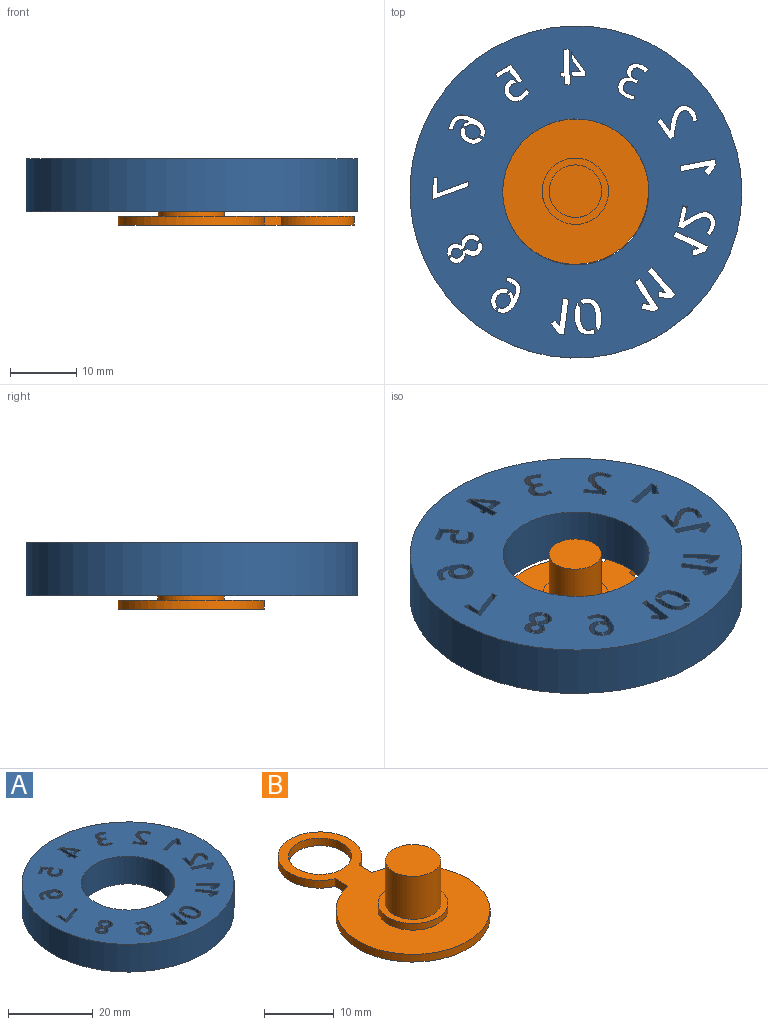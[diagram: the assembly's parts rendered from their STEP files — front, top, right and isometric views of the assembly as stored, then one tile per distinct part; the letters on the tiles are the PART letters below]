
ASSEMBLY  parts=2 mates=1
PART A: 389 faces, bbox 50x50x8 mm
  f0: plane 50x50mm, normal (0,0,1), area 1468.7mm2, adj f2,f3,f4,f5,f6,f7,f8,f9
  f1: plane 50x50mm, normal (0,0,-1), area 1468.7mm2, adj f2,f3,f4,f5,f6,f7,f8,f9
  f2: cylinder r=11mm len=22mm, axis (0,0,-1), area 552.9mm2, adj f0,f1
  f3: cylinder r=25mm len=50mm, axis (0,0,-1), area 1256.6mm2, adj f0,f1
  f4: plane 8x1.59mm, normal (-0.83,0.56,0), area 15.4mm2, adj f0,f1,f5,f10
  f5: plane 8x0.73mm, normal (0.56,0.83,0), area 7.1mm2, adj f0,f1,f4,f6
  f6: plane 8x0.86mm, normal (0.83,-0.56,0), area 8.3mm2, adj f0,f1,f5,f7
  f7: plane 8x4.05mm, normal (-0.19,0.98,0), area 33mm2, adj f0,f1,f6,f8
  f8: plane 8x0.88mm, normal (0.98,0.19,0), area 7.1mm2, adj f0,f1,f7,f9
  f9: plane 8x5.28mm, normal (0.19,-0.98,0), area 43mm2, adj f0,f1,f8,f10
  f10: plane 8x0.88mm, normal (-0.98,-0.19,0), area 7.1mm2, adj f0,f1,f4,f9
  f11: plane 8x1.81mm, normal (-0.34,0.94,0), area 15.4mm2, adj f0,f1,f12,f17
  f12: plane 8x0.83mm, normal (0.94,0.34,0), area 7.1mm2, adj f0,f1,f11,f13
  f13: plane 8x0.98mm, normal (0.34,-0.94,0), area 8.3mm2, adj f0,f1,f12,f14
  f14: plane 8x3.74mm, normal (0.42,0.91,0), area 33mm2, adj f0,f1,f13,f15
  f15: plane 8x0.81mm, normal (0.91,-0.42,0), area 7.1mm2, adj f0,f1,f14,f16
  f16: plane 8x4.87mm, normal (-0.42,-0.91,0), area 43mm2, adj f0,f1,f15,f17
  f17: plane 8x0.81mm, normal (-0.91,0.42,0), area 7.1mm2, adj f0,f1,f11,f16
  f18: plane 8x0.47mm, normal (0.63,0.78,0), area 4.8mm2, adj f0,f1,f28,f29
  f19: plane 8x0.79mm, normal (0.23,0.97,0), area 6.5mm2, adj f0,f1,f20,f42
  f20: plane 8x3.25mm, normal (0.97,-0.23,0), area 26.7mm2, adj f0,f1,f19,f21
  f21: plane 8x0.69mm, normal (-0.23,-0.97,0), area 5.7mm2, adj f0,f1,f20,f22
  f22: plane 8x2.22mm, normal (-0.97,0.23,0), area 18.3mm2, adj f0,f1,f21,f43
  f23: extruded ~8x0.63mm, area 5.5mm2, adj f0,f1,f24,f50
  f24: extruded ~8x0.83mm, area 6.7mm2, adj f0,f1,f23,f25
  f25: extruded ~8x0.36mm, area 3mm2, adj f0,f1,f24,f26
  f26: extruded ~8x0.38mm, area 3.4mm2, adj f0,f1,f25,f27
  f27: extruded ~8x0.36mm, area 3.4mm2, adj f0,f1,f26,f28
  f28: extruded ~8x0.28mm, area 3.1mm2, adj f0,f1,f18,f27
  f29: extruded ~8x0.2mm, area 2.1mm2, adj f0,f1,f18,f30
  f30: extruded ~8x0.22mm, area 2.1mm2, adj f0,f1,f29,f31
  f31: extruded ~8x0.3mm, area 2.6mm2, adj f0,f1,f30,f32
  f32: extruded ~8x0.45mm, area 3.8mm2, adj f0,f1,f31,f33
  f33: extruded ~8x0.31mm, area 2.5mm2, adj f0,f1,f32,f34
  f34: extruded ~8x0.33mm, area 2.7mm2, adj f0,f1,f33,f35
  f35: extruded ~8x0.29mm, area 2.9mm2, adj f0,f1,f34,f36
  f36: extruded ~8x0.39mm, area 3.5mm2, adj f0,f1,f35,f37
  f37: extruded ~8x0.54mm, area 4.4mm2, adj f0,f1,f36,f38
  f38: extruded ~8x0.63mm, area 5.4mm2, adj f0,f1,f37,f39
  f39: extruded ~8x0.67mm, area 6mm2, adj f0,f1,f38,f40
  f40: extruded ~8x0.64mm, area 6mm2, adj f0,f1,f39,f41
  f41: extruded ~8x0.55mm, area 5.4mm2, adj f0,f1,f40,f42
  f42: extruded ~8x0.39mm, area 3.9mm2, adj f0,f1,f19,f41
  f43: extruded ~8x0.41mm, area 3.9mm2, adj f0,f1,f22,f44
  f44: extruded ~8x0.54mm, area 5.1mm2, adj f0,f1,f43,f45
  f45: extruded ~8x0.62mm, area 5.7mm2, adj f0,f1,f44,f46
  f46: extruded ~8x0.66mm, area 5.8mm2, adj f0,f1,f45,f47
  f47: extruded ~8x0.66mm, area 5.5mm2, adj f0,f1,f46,f48
  f48: extruded ~8x0.6mm, area 4.8mm2, adj f0,f1,f47,f49
  f49: extruded ~8x0.52mm, area 4.6mm2, adj f0,f1,f48,f50
  f50: extruded ~8x0.44mm, area 5mm2, adj f0,f1,f23,f49
  f51: plane 8x1.89mm, normal (0.21,0.98,0), area 15.4mm2, adj f0,f1,f52,f57
  f52: plane 8x0.87mm, normal (0.98,-0.21,0), area 7.1mm2, adj f0,f1,f51,f53
  f53: plane 8x1.02mm, normal (-0.21,-0.98,0), area 8.3mm2, adj f0,f1,f52,f54
  f54: plane 8x3.46mm, normal (0.84,0.54,0), area 33mm2, adj f0,f1,f53,f55
  f55: plane 8x0.75mm, normal (0.54,-0.84,0), area 7.1mm2, adj f0,f1,f54,f56
  f56: plane 8x4.52mm, normal (-0.84,-0.54,0), area 43mm2, adj f0,f1,f55,f57
  f57: plane 8x0.75mm, normal (-0.54,0.84,0), area 7.1mm2, adj f0,f1,f51,f56
  f58: plane 8x1.93mm, normal (0.06,1,0), area 15.4mm2, adj f0,f1,f59,f64
  f59: plane 8x0.89mm, normal (1,-0.06,0), area 7.1mm2, adj f0,f1,f58,f60
  f60: plane 8x1.04mm, normal (-0.06,-1,0), area 8.3mm2, adj f0,f1,f59,f61
  f61: plane 8x3.08mm, normal (0.75,0.66,0), area 33mm2, adj f0,f1,f60,f62
  f62: plane 8x0.67mm, normal (0.66,-0.75,0), area 7.1mm2, adj f0,f1,f61,f63
  f63: plane 8x4.02mm, normal (-0.75,-0.66,0), area 43mm2, adj f0,f1,f62,f64
  f64: plane 8x0.67mm, normal (-0.66,0.75,0), area 7.1mm2, adj f0,f1,f58,f63
  f65: plane 8x0.59mm, normal (-0.83,0.56,0), area 5.7mm2, adj f0,f1,f69,f70
  f66: plane 8x0.55mm, normal (-0.83,0.56,0), area 5.3mm2, adj f0,f1,f77,f78
  f67: extruded ~8x0.62mm, area 6.5mm2, adj f0,f1,f68,f78
  f68: extruded ~8x0.78mm, area 6.6mm2, adj f0,f1,f67,f69
  f69: extruded ~8x0.66mm, area 5.9mm2, adj f0,f1,f65,f68
  f70: extruded ~8x0.42mm, area 4.5mm2, adj f0,f1,f65,f71
  f71: extruded ~8x0.57mm, area 5mm2, adj f0,f1,f70,f72
  f72: extruded ~8x0.71mm, area 5.7mm2, adj f0,f1,f71,f73
  f73: extruded ~8x0.82mm, area 7.2mm2, adj f0,f1,f72,f74
  f74: extruded ~8x0.44mm, area 4.9mm2, adj f0,f1,f73,f75
  f75: extruded ~8x0.57mm, area 5.1mm2, adj f0,f1,f74,f76
  f76: extruded ~8x0.65mm, area 5.2mm2, adj f0,f1,f75,f77
  f77: extruded ~8x0.65mm, area 5.6mm2, adj f0,f1,f66,f76
  f78: extruded ~8x0.71mm, area 5.8mm2, adj f0,f1,f66,f67
  f79: plane 8x0.63mm, normal (0.46,-0.89,0), area 5.7mm2, adj f0,f1,f87,f88
  f80: plane 8x0.81mm, normal (0.46,-0.89,0), area 7.2mm2, adj f0,f1,f92,f93
  f81: plane 8x0.62mm, normal (0.46,-0.89,0), area 5.5mm2, adj f0,f1,f98,f99
  f82: extruded ~8x0.3mm, area 2.9mm2, adj f0,f1,f83,f108
  f83: extruded ~8x0.27mm, area 2.8mm2, adj f0,f1,f82,f84
  f84: extruded ~8x0.48mm, area 4.1mm2, adj f0,f1,f83,f85
  f85: extruded ~8x0.49mm, area 4mm2, adj f0,f1,f84,f86
  f86: extruded ~8x0.47mm, area 4.2mm2, adj f0,f1,f85,f87
  f87: extruded ~8x0.49mm, area 5.1mm2, adj f0,f1,f79,f86
  f88: extruded ~8x0.34mm, area 3.7mm2, adj f0,f1,f79,f89
  f89: extruded ~8x0.55mm, area 4.6mm2, adj f0,f1,f88,f90
  f90: extruded ~8x0.39mm, area 4.5mm2, adj f0,f1,f89,f91
  f91: extruded ~8x0.49mm, area 4.1mm2, adj f0,f1,f90,f92
  f92: extruded ~8x0.09mm, area 0.8mm2, adj f0,f1,f80,f91
  f93: extruded ~8x0.62mm, area 5.5mm2, adj f0,f1,f80,f94
  f94: extruded ~8x0.56mm, area 4.6mm2, adj f0,f1,f93,f95
  f95: extruded ~8x0.19mm, area 2mm2, adj f0,f1,f94,f96
  f96: extruded ~8x0.24mm, area 2.2mm2, adj f0,f1,f95,f97
  f97: extruded ~8x0.29mm, area 2.3mm2, adj f0,f1,f96,f98
  f98: extruded ~8x0.31mm, area 2.5mm2, adj f0,f1,f81,f97
  f99: extruded ~8x0.59mm, area 4.9mm2, adj f0,f1,f81,f100
  f100: extruded ~8x0.58mm, area 4.6mm2, adj f0,f1,f99,f101
  f101: extruded ~8x0.51mm, area 4.6mm2, adj f0,f1,f100,f102
  f102: extruded ~8x0.48mm, area 5mm2, adj f0,f1,f101,f103
  f103: extruded ~8x0.43mm, area 3.6mm2, adj f0,f1,f102,f104
  f104: extruded ~8x0.43mm, area 3.5mm2, adj f0,f1,f103,f105
  f105: extruded ~8x0.42mm, area 3.6mm2, adj f0,f1,f104,f106
  f106: extruded ~8x0.41mm, area 3.7mm2, adj f0,f1,f105,f107
  f107: extruded ~8x0.37mm, area 3mm2, adj f0,f1,f106,f108
  f108: extruded ~8x0.36mm, area 3.1mm2, adj f0,f1,f82,f107
  f109: plane 8x0.62mm, normal (-0.46,0.89,0), area 5.5mm2, adj f0,f1,f116,f117
  f110: plane 8x0.11mm, normal (-0.55,-0.83,0), area 1.1mm2, adj f0,f1,f111,f122
  f111: plane 8x0.79mm, normal (-0.46,0.89,0), area 7.1mm2, adj f0,f1,f110,f123
  f112: plane 8x0.63mm, normal (-0.46,0.89,0), area 5.7mm2, adj f0,f1,f126,f127
  f113: extruded ~8x0.84mm, area 7mm2, adj f0,f1,f114,f132
  f114: extruded ~8x0.69mm, area 7.7mm2, adj f0,f1,f113,f115
  f115: extruded ~8x1.1mm, area 9.1mm2, adj f0,f1,f114,f116
  f116: extruded ~8x0.9mm, area 10mm2, adj f0,f1,f109,f115
  f117: extruded ~8x0.5mm, area 5mm2, adj f0,f1,f109,f118
  f118: extruded ~8x0.57mm, area 4.7mm2, adj f0,f1,f117,f119
  f119: extruded ~8x0.29mm, area 3mm2, adj f0,f1,f118,f120
  f120: extruded ~8x0.28mm, area 2.7mm2, adj f0,f1,f119,f121
  f121: extruded ~8x0.29mm, area 2.5mm2, adj f0,f1,f120,f122
  f122: extruded ~8x0.27mm, area 2.2mm2, adj f0,f1,f110,f121
  f123: extruded ~8x0.48mm, area 4.4mm2, adj f0,f1,f111,f124
  f124: extruded ~8x0.4mm, area 3.3mm2, adj f0,f1,f123,f125
  f125: extruded ~8x0.37mm, area 4.2mm2, adj f0,f1,f124,f126
  f126: extruded ~8x0.5mm, area 4.1mm2, adj f0,f1,f112,f125
  f127: extruded ~8x0.54mm, area 4.5mm2, adj f0,f1,f112,f128
  f128: extruded ~8x0.51mm, area 4.1mm2, adj f0,f1,f127,f129
  f129: extruded ~8x0.45mm, area 4.1mm2, adj f0,f1,f128,f130
  f130: extruded ~8x0.45mm, area 4.6mm2, adj f0,f1,f129,f131
  f131: extruded ~8x0.69mm, area 5.7mm2, adj f0,f1,f130,f132
  f132: extruded ~8x0.69mm, area 5.9mm2, adj f0,f1,f113,f131
  f133: plane 8x3.38mm, normal (1,-0.02,0), area 27mm2, adj f0,f1,f134,f138
  f134: plane 8x0.71mm, normal (-0.02,-1,0), area 5.7mm2, adj f0,f1,f133,f135
  f135: plane 8x2.34mm, normal (-1,0.02,0), area 18.7mm2, adj f0,f1,f134,f136
  f136: plane 8x4.71mm, normal (0.35,-0.94,0), area 40.2mm2, adj f0,f1,f135,f137
  f137: plane 8x0.82mm, normal (-1,0.02,0), area 6.5mm2, adj f0,f1,f136,f138
  f138: plane 8x5.43mm, normal (-0.34,0.94,0), area 46.1mm2, adj f0,f1,f133,f137
  f139: plane 8x0.53mm, normal (0.83,-0.56,0), area 5.1mm2, adj f0,f1,f148,f149
  f140: plane 8x0.66mm, normal (0.99,-0.15,0), area 5.3mm2, adj f0,f1,f158,f159
  f141: plane 8x0.6mm, normal (0.83,-0.56,0), area 5.7mm2, adj f0,f1,f168,f169
  f142: extruded ~8x0.38mm, area 3.1mm2, adj f0,f1,f143,f169
  f143: extruded ~8x0.36mm, area 3.3mm2, adj f0,f1,f142,f144
  f144: extruded ~8x0.33mm, area 3.6mm2, adj f0,f1,f143,f145
  f145: extruded ~8x0.4mm, area 3.5mm2, adj f0,f1,f144,f146
  f146: extruded ~8x0.4mm, area 3.2mm2, adj f0,f1,f145,f147
  f147: extruded ~8x0.36mm, area 3mm2, adj f0,f1,f146,f148
  f148: extruded ~8x0.3mm, area 3.1mm2, adj f0,f1,f139,f147
  f149: extruded ~8x0.43mm, area 4.5mm2, adj f0,f1,f139,f150
  f150: extruded ~8x0.4mm, area 3.4mm2, adj f0,f1,f149,f151
  f151: extruded ~8x0.02mm, area 0.2mm2, adj f0,f1,f150,f152
  f152: extruded ~8x0.02mm, area 0.3mm2, adj f0,f1,f151,f153
  f153: extruded ~8x0.53mm, area 4.8mm2, adj f0,f1,f152,f154
  f154: extruded ~8x0.53mm, area 4.3mm2, adj f0,f1,f153,f155
  f155: extruded ~8x0.49mm, area 4mm2, adj f0,f1,f154,f156
  f156: extruded ~8x0.4mm, area 4.3mm2, adj f0,f1,f155,f157
  f157: extruded ~8x0.5mm, area 4.6mm2, adj f0,f1,f156,f158
  f158: extruded ~8x0.47mm, area 3.9mm2, adj f0,f1,f140,f157
  f159: extruded ~8x0.64mm, area 5.3mm2, adj f0,f1,f140,f160
  f160: extruded ~8x0.67mm, area 6.1mm2, adj f0,f1,f159,f161
  f161: extruded ~8x0.51mm, area 5.7mm2, adj f0,f1,f160,f162
  f162: extruded ~8x0.79mm, area 6.6mm2, adj f0,f1,f161,f163
  f163: extruded ~8x1.09mm, area 8.9mm2, adj f0,f1,f162,f164
  f164: extruded ~8x1.43mm, area 12.9mm2, adj f0,f1,f163,f165
  f165: extruded ~8x0.65mm, area 6.8mm2, adj f0,f1,f164,f166
  f166: extruded ~8x0.64mm, area 6mm2, adj f0,f1,f165,f167
  f167: extruded ~8x0.71mm, area 5.8mm2, adj f0,f1,f166,f168
  f168: extruded ~8x0.75mm, area 6.4mm2, adj f0,f1,f141,f167
  f169: extruded ~8x0.37mm, area 3.1mm2, adj f0,f1,f141,f142
  f170: plane 8x1.53mm, normal (0.79,0.61,0), area 15.4mm2, adj f0,f1,f171,f176
  f171: plane 8x0.7mm, normal (0.61,-0.79,0), area 7.1mm2, adj f0,f1,f170,f172
  f172: plane 8x0.82mm, normal (-0.79,-0.61,0), area 8.3mm2, adj f0,f1,f171,f173
  f173: plane 8x4.09mm, normal (0.99,-0.13,0), area 33mm2, adj f0,f1,f172,f174
  f174: plane 8x0.88mm, normal (-0.13,-0.99,0), area 7.1mm2, adj f0,f1,f173,f175
  f175: plane 8x5.33mm, normal (-0.99,0.13,0), area 43mm2, adj f0,f1,f174,f176
  f176: plane 8x0.88mm, normal (0.13,0.99,0), area 7.1mm2, adj f0,f1,f170,f175
  f177: plane 8x0.66mm, normal (0.86,0.51,0), area 6.1mm2, adj f0,f1,f185,f186
  f178: plane 8x0.8mm, normal (0.86,0.51,0), area 7.5mm2, adj f0,f1,f192,f193
  f179: extruded ~8x0.6mm, area 4.9mm2, adj f0,f1,f180,f193
  f180: extruded ~8x0.81mm, area 6.4mm2, adj f0,f1,f179,f181
  f181: extruded ~8x0.94mm, area 7.7mm2, adj f0,f1,f180,f182
  f182: extruded ~8x0.61mm, area 5.4mm2, adj f0,f1,f181,f183
  f183: extruded ~8x0.41mm, area 4.1mm2, adj f0,f1,f182,f184
  f184: extruded ~8x0.5mm, area 4.1mm2, adj f0,f1,f183,f185
  f185: extruded ~8x0.55mm, area 4.9mm2, adj f0,f1,f177,f184
  f186: extruded ~8x0.89mm, area 7.6mm2, adj f0,f1,f177,f187
  f187: extruded ~8x0.87mm, area 7.1mm2, adj f0,f1,f186,f188
  f188: extruded ~8x0.7mm, area 6.7mm2, adj f0,f1,f187,f189
  f189: extruded ~8x0.82mm, area 7.7mm2, adj f0,f1,f188,f190
  f190: extruded ~8x1.18mm, area 9.7mm2, adj f0,f1,f189,f191
  f191: extruded ~8x1.36mm, area 10.9mm2, adj f0,f1,f190,f192
  f192: extruded ~8x0.95mm, area 8.5mm2, adj f0,f1,f178,f191
  f193: extruded ~8x0.02mm, area 0.1mm2, adj f0,f1,f178,f179
  f194: plane 8x0.81mm, normal (-0.86,-0.51,0), area 7.5mm2, adj f0,f1,f202,f203
  f195: plane 8x0.65mm, normal (-0.86,-0.51,0), area 6.1mm2, adj f0,f1,f196,f209
  f196: extruded ~8x0.86mm, area 7.3mm2, adj f0,f1,f195,f197
  f197: extruded ~8x0.87mm, area 7.1mm2, adj f0,f1,f196,f198
  f198: extruded ~8x0.7mm, area 6.7mm2, adj f0,f1,f197,f199
  f199: extruded ~8x0.81mm, area 7.6mm2, adj f0,f1,f198,f200
  f200: extruded ~8x1.17mm, area 9.6mm2, adj f0,f1,f199,f201
  f201: extruded ~8x1.34mm, area 10.8mm2, adj f0,f1,f200,f202
  f202: extruded ~8x0.94mm, area 8.3mm2, adj f0,f1,f194,f201
  f203: extruded ~8x0.6mm, area 4.8mm2, adj f0,f1,f194,f204
  f204: extruded ~8x0.79mm, area 6.3mm2, adj f0,f1,f203,f205
  f205: extruded ~8x0.94mm, area 7.6mm2, adj f0,f1,f204,f206
  f206: extruded ~8x0.61mm, area 5.4mm2, adj f0,f1,f205,f207
  f207: extruded ~8x0.4mm, area 4.1mm2, adj f0,f1,f206,f208
  f208: extruded ~8x0.5mm, area 4mm2, adj f0,f1,f207,f209
  f209: extruded ~8x0.52mm, area 4.6mm2, adj f0,f1,f195,f208
  f210: plane 8x0.66mm, normal (0.1,1,0), area 5.3mm2, adj f0,f1,f213,f240
  f211: plane 8x0.62mm, normal (0.51,0.86,0), area 5.7mm2, adj f0,f1,f222,f223
  f212: plane 8x0.55mm, normal (0.51,0.86,0), area 5.1mm2, adj f0,f1,f230,f231
  f213: extruded ~8x0.64mm, area 5.3mm2, adj f0,f1,f210,f214
  f214: extruded ~8x0.69mm, area 6.2mm2, adj f0,f1,f213,f215
  f215: extruded ~8x0.52mm, area 5.7mm2, adj f0,f1,f214,f216
  f216: extruded ~8x0.77mm, area 6.6mm2, adj f0,f1,f215,f217
  f217: extruded ~8x1.1mm, area 8.9mm2, adj f0,f1,f216,f218
  f218: extruded ~8x1.47mm, area 12.9mm2, adj f0,f1,f217,f219
  f219: extruded ~8x0.68mm, area 6.8mm2, adj f0,f1,f218,f220
  f220: extruded ~8x0.62mm, area 6mm2, adj f0,f1,f219,f221
  f221: extruded ~8x0.71mm, area 5.8mm2, adj f0,f1,f220,f222
  f222: extruded ~8x0.77mm, area 6.5mm2, adj f0,f1,f211,f221
  f223: extruded ~8x0.38mm, area 3.1mm2, adj f0,f1,f211,f224
  f224: extruded ~8x0.38mm, area 3.1mm2, adj f0,f1,f223,f225
  f225: extruded ~8x0.35mm, area 3.3mm2, adj f0,f1,f224,f226
  f226: extruded ~8x0.35mm, area 3.6mm2, adj f0,f1,f225,f227
  f227: extruded ~8x0.41mm, area 3.5mm2, adj f0,f1,f226,f228
  f228: extruded ~8x0.4mm, area 3.2mm2, adj f0,f1,f227,f229
  f229: extruded ~8x0.36mm, area 3mm2, adj f0,f1,f228,f230
  f230: extruded ~8x0.29mm, area 3.1mm2, adj f0,f1,f212,f229
  f231: extruded ~8x0.41mm, area 4.5mm2, adj f0,f1,f212,f232
  f232: extruded ~8x0.4mm, area 3.4mm2, adj f0,f1,f231,f233
  f233: extruded ~8x0.02mm, area 0.2mm2, adj f0,f1,f232,f234
  f234: extruded ~8x0.02mm, area 0.3mm2, adj f0,f1,f233,f235
  f235: extruded ~8x0.55mm, area 4.8mm2, adj f0,f1,f234,f236
  f236: extruded ~8x0.54mm, area 4.4mm2, adj f0,f1,f235,f237
  f237: extruded ~8x0.49mm, area 4.1mm2, adj f0,f1,f236,f238
  f238: extruded ~8x0.38mm, area 4.3mm2, adj f0,f1,f237,f239
  f239: extruded ~8x0.51mm, area 4.6mm2, adj f0,f1,f238,f240
  f240: extruded ~8x0.47mm, area 3.9mm2, adj f0,f1,f210,f239
  f241: plane 8x0.62mm, normal (-0.51,-0.86,0), area 5.7mm2, adj f0,f1,f245,f246
  f242: plane 8x0.57mm, normal (-0.51,-0.86,0), area 5.3mm2, adj f0,f1,f253,f254
  f243: extruded ~8x0.58mm, area 6.4mm2, adj f0,f1,f244,f254
  f244: extruded ~8x0.79mm, area 6.6mm2, adj f0,f1,f243,f245
  f245: extruded ~8x0.64mm, area 5.9mm2, adj f0,f1,f241,f244
  f246: extruded ~8x0.4mm, area 4.5mm2, adj f0,f1,f241,f247
  f247: extruded ~8x0.56mm, area 5mm2, adj f0,f1,f246,f248
  f248: extruded ~8x0.7mm, area 5.7mm2, adj f0,f1,f247,f249
  f249: extruded ~8x0.83mm, area 7.2mm2, adj f0,f1,f248,f250
  f250: extruded ~8x0.46mm, area 4.9mm2, adj f0,f1,f249,f251
  f251: extruded ~8x0.55mm, area 5.1mm2, adj f0,f1,f250,f252
  f252: extruded ~8x0.64mm, area 5.2mm2, adj f0,f1,f251,f253
  f253: extruded ~8x0.66mm, area 5.5mm2, adj f0,f1,f242,f252
  f254: extruded ~8x0.71mm, area 5.9mm2, adj f0,f1,f242,f243
  f255: plane 8x0.58mm, normal (-0.79,-0.61,0), area 5.8mm2, adj f0,f1,f257,f280
  f256: plane 8x0.63mm, normal (-0.86,-0.51,0), area 5.8mm2, adj f0,f1,f266,f267
  f257: extruded ~8x0.25mm, area 2.1mm2, adj f0,f1,f255,f258
  f258: extruded ~8x0.25mm, area 2.2mm2, adj f0,f1,f257,f259
  f259: extruded ~8x0.56mm, area 6mm2, adj f0,f1,f258,f260
  f260: extruded ~8x0.7mm, area 5.8mm2, adj f0,f1,f259,f261
  f261: extruded ~8x0.7mm, area 7.5mm2, adj f0,f1,f260,f262
  f262: extruded ~8x0.87mm, area 7.3mm2, adj f0,f1,f261,f263
  f263: extruded ~8x0.29mm, area 2.9mm2, adj f0,f1,f262,f264
  f264: extruded ~8x0.29mm, area 3.1mm2, adj f0,f1,f263,f265
  f265: extruded ~8x0.29mm, area 2.9mm2, adj f0,f1,f264,f266
  f266: extruded ~8x0.25mm, area 2.4mm2, adj f0,f1,f256,f265
  f267: extruded ~8x0.19mm, area 1.9mm2, adj f0,f1,f256,f268
  f268: extruded ~8x0.27mm, area 2.8mm2, adj f0,f1,f267,f269
  f269: extruded ~8x0.3mm, area 3.4mm2, adj f0,f1,f268,f270
  f270: extruded ~8x0.39mm, area 3.8mm2, adj f0,f1,f269,f271
  f271: extruded ~8x0.49mm, area 4.3mm2, adj f0,f1,f270,f272
  f272: extruded ~8x0.64mm, area 5.2mm2, adj f0,f1,f271,f273
  f273: extruded ~8x0.69mm, area 5.9mm2, adj f0,f1,f272,f274
  f274: extruded ~8x0.72mm, area 7.9mm2, adj f0,f1,f273,f275
  f275: extruded ~8x0.56mm, area 4.8mm2, adj f0,f1,f274,f276
  f276: extruded ~8x0.6mm, area 4.9mm2, adj f0,f1,f275,f277
  f277: extruded ~8x0.57mm, area 5.1mm2, adj f0,f1,f276,f278
  f278: extruded ~8x0.52mm, area 5.6mm2, adj f0,f1,f277,f279
  f279: extruded ~8x0.22mm, area 2mm2, adj f0,f1,f278,f280
  f280: extruded ~8x0.29mm, area 2.5mm2, adj f0,f1,f255,f279
  f281: plane 8x1.73mm, normal (-0.51,0.86,0), area 16.1mm2, adj f0,f1,f282,f290
  f282: plane 8x0.62mm, normal (0.86,0.51,0), area 5.7mm2, adj f0,f1,f281,f283
  f283: plane 8x2.29mm, normal (0.51,-0.86,0), area 21.3mm2, adj f0,f1,f282,f291
  f284: plane 8x0.59mm, normal (-0.51,0.86,0), area 5.5mm2, adj f0,f1,f285,f295
  f285: plane 8x0.23mm, normal (0.79,0.61,0), area 2.4mm2, adj f0,f1,f284,f286
  f286: plane 8x0.39mm, normal (0.79,0.61,0), area 3.9mm2, adj f0,f1,f285,f287
  f287: extruded ~8x0.03mm, area 0.3mm2, adj f0,f1,f286,f288
  f288: extruded ~8x0.14mm, area 1.4mm2, adj f0,f1,f287,f289
  f289: extruded ~8x0.35mm, area 3.6mm2, adj f0,f1,f288,f290
  f290: extruded ~8x0.66mm, area 6.8mm2, adj f0,f1,f281,f289
  f291: extruded ~8x1.1mm, area 11.1mm2, adj f0,f1,f283,f292
  f292: extruded ~8x0.43mm, area 4.3mm2, adj f0,f1,f291,f293
  f293: extruded ~8x0.39mm, area 3.9mm2, adj f0,f1,f292,f294
  f294: extruded ~8x0.31mm, area 3.1mm2, adj f0,f1,f293,f295
  f295: extruded ~8x0.18mm, area 1.8mm2, adj f0,f1,f284,f294
  f296: plane 8x1.25mm, normal (0.03,-1,0), area 10mm2, adj f0,f1,f297,f302
  f297: plane 8x1.91mm, normal (0.82,0.57,0), area 18.5mm2, adj f0,f1,f296,f298
  f298: plane 8x1.04mm, normal (1,0.03,0), area 8.3mm2, adj f0,f1,f297,f299
  f299: plane 8x2.93mm, normal (-0.81,-0.59,0), area 28.9mm2, adj f0,f1,f298,f300
  f300: plane 8x0.69mm, normal (-1,-0.03,0), area 5.5mm2, adj f0,f1,f299,f301
  f301: plane 8x2.03mm, normal (-0.03,1,0), area 16.2mm2, adj f0,f1,f300,f302
  f302: plane 8x0.69mm, normal (1,0.03,0), area 5.5mm2, adj f0,f1,f296,f301
  f303: plane 8x5.37mm, normal (-1,-0.03,0), area 43mm2, adj f0,f1,f304,f310
  f304: plane 8x0.89mm, normal (-0.03,1,0), area 7.1mm2, adj f0,f1,f303,f305
  f305: plane 8x1.25mm, normal (1,0.03,0), area 10mm2, adj f0,f1,f304,f306
  f306: plane 8x0.56mm, normal (-0.03,1,0), area 4.5mm2, adj f0,f1,f305,f307
  f307: plane 8x0.69mm, normal (1,0.03,0), area 5.5mm2, adj f0,f1,f306,f308
  f308: plane 8x0.56mm, normal (0.03,-1,0), area 4.5mm2, adj f0,f1,f307,f309
  f309: plane 8x3.43mm, normal (1,0.03,0), area 27.4mm2, adj f0,f1,f308,f310
  f310: plane 8x0.89mm, normal (0.03,-1,0), area 7.1mm2, adj f0,f1,f303,f309
  f311: plane 8x0.65mm, normal (-0.99,0.16,0), area 5.3mm2, adj f0,f1,f323,f324
  f312: plane 8x0.52mm, normal (-0.67,0.74,0), area 5.6mm2, adj f0,f1,f345,f346
  f313: plane 8x0.44mm, normal (-0.45,-0.89,0), area 4mm2, adj f0,f1,f314,f355
  f314: plane 8x0.53mm, normal (-0.89,0.46,0), area 4.7mm2, adj f0,f1,f313,f315
  f315: plane 8x0.66mm, normal (0.45,0.89,0), area 5.9mm2, adj f0,f1,f314,f316
  f316: extruded ~8x0.71mm, area 5.9mm2, adj f0,f1,f315,f317
  f317: extruded ~8x0.5mm, area 5.7mm2, adj f0,f1,f316,f318
  f318: extruded ~8x0.73mm, area 6mm2, adj f0,f1,f317,f319
  f319: extruded ~8x0.58mm, area 6.6mm2, adj f0,f1,f318,f320
  f320: extruded ~8x0.49mm, area 4.3mm2, adj f0,f1,f319,f321
  f321: extruded ~8x0.3mm, area 2.5mm2, adj f0,f1,f320,f322
  f322: extruded ~8x0.19mm, area 1.5mm2, adj f0,f1,f321,f323
  f323: extruded ~8x0.15mm, area 1.2mm2, adj f0,f1,f311,f322
  f324: extruded ~8x0.52mm, area 4.2mm2, adj f0,f1,f311,f325
  f325: extruded ~8x0.9mm, area 7.8mm2, adj f0,f1,f324,f326
  f326: extruded ~8x0.21mm, area 2mm2, adj f0,f1,f325,f327
  f327: extruded ~8x0.28mm, area 2.8mm2, adj f0,f1,f326,f328
  f328: extruded ~8x0.32mm, area 3.4mm2, adj f0,f1,f327,f329
  f329: extruded ~8x0.41mm, area 3.7mm2, adj f0,f1,f328,f330
  f330: extruded ~8x0.51mm, area 4.1mm2, adj f0,f1,f329,f331
  f331: extruded ~8x0.61mm, area 5.1mm2, adj f0,f1,f330,f332
  f332: extruded ~8x0.43mm, area 4.3mm2, adj f0,f1,f331,f333
  f333: extruded ~8x0.4mm, area 3.7mm2, adj f0,f1,f332,f334
  f334: extruded ~8x0.41mm, area 3.3mm2, adj f0,f1,f333,f335
  f335: extruded ~8x0.36mm, area 2.9mm2, adj f0,f1,f334,f336
  f336: extruded ~8x0.24mm, area 2.5mm2, adj f0,f1,f335,f337
  f337: extruded ~8x0.33mm, area 2.9mm2, adj f0,f1,f336,f338
  f338: extruded ~8x0.38mm, area 3.1mm2, adj f0,f1,f337,f339
  f339: extruded ~8x0.4mm, area 3.4mm2, adj f0,f1,f338,f340
  f340: extruded ~8x0.54mm, area 5.5mm2, adj f0,f1,f339,f341
  f341: extruded ~8x0.54mm, area 4.8mm2, adj f0,f1,f340,f342
  f342: extruded ~8x0.6mm, area 4.8mm2, adj f0,f1,f341,f343
  f343: extruded ~8x0.62mm, area 5.3mm2, adj f0,f1,f342,f344
  f344: extruded ~8x0.64mm, area 6mm2, adj f0,f1,f343,f345
  f345: extruded ~8x0.34mm, area 3.6mm2, adj f0,f1,f312,f344
  f346: extruded ~8x0.23mm, area 2.6mm2, adj f0,f1,f312,f347
  f347: extruded ~8x0.45mm, area 4.3mm2, adj f0,f1,f346,f348
  f348: extruded ~8x0.5mm, area 4.3mm2, adj f0,f1,f347,f349
  f349: extruded ~8x0.35mm, area 2.8mm2, adj f0,f1,f348,f350
  f350: extruded ~8x0.23mm, area 2.4mm2, adj f0,f1,f349,f351
  f351: extruded ~8x0.24mm, area 2.2mm2, adj f0,f1,f350,f352
  f352: extruded ~8x0.49mm, area 4.1mm2, adj f0,f1,f351,f353
  f353: extruded ~8x0.33mm, area 2.8mm2, adj f0,f1,f352,f354
  f354: extruded ~8x0.24mm, area 2.6mm2, adj f0,f1,f353,f355
  f355: extruded ~8x0.29mm, area 2.6mm2, adj f0,f1,f313,f354
  f356: plane 8x0.59mm, normal (-0.17,0.99,0), area 4.8mm2, adj f0,f1,f366,f367
  f357: plane 8x0.67mm, normal (-0.57,0.82,0), area 6.5mm2, adj f0,f1,f358,f380
  f358: plane 8x2.74mm, normal (0.82,0.57,0), area 26.7mm2, adj f0,f1,f357,f359
  f359: plane 8x0.58mm, normal (0.57,-0.82,0), area 5.7mm2, adj f0,f1,f358,f360
  f360: plane 8x1.87mm, normal (-0.82,-0.57,0), area 18.3mm2, adj f0,f1,f359,f381
  f361: extruded ~8x0.64mm, area 5.5mm2, adj f0,f1,f362,f388
  f362: extruded ~8x0.59mm, area 6.7mm2, adj f0,f1,f361,f363
  f363: extruded ~8x0.33mm, area 3mm2, adj f0,f1,f362,f364
  f364: extruded ~8x0.39mm, area 3.4mm2, adj f0,f1,f363,f365
  f365: extruded ~8x0.42mm, area 3.4mm2, adj f0,f1,f364,f366
  f366: extruded ~8x0.39mm, area 3.1mm2, adj f0,f1,f356,f365
  f367: extruded ~8x0.27mm, area 2.1mm2, adj f0,f1,f356,f368
  f368: extruded ~8x0.26mm, area 2.1mm2, adj f0,f1,f367,f369
  f369: extruded ~8x0.3mm, area 2.6mm2, adj f0,f1,f368,f370
  f370: extruded ~8x0.4mm, area 3.8mm2, adj f0,f1,f369,f371
  f371: extruded ~8x0.23mm, area 2.5mm2, adj f0,f1,f370,f372
  f372: extruded ~8x0.3mm, area 2.7mm2, adj f0,f1,f371,f373
  f373: extruded ~8x0.36mm, area 2.9mm2, adj f0,f1,f372,f374
  f374: extruded ~8x0.4mm, area 3.5mm2, adj f0,f1,f373,f375
  f375: extruded ~8x0.42mm, area 4.4mm2, adj f0,f1,f374,f376
  f376: extruded ~8x0.62mm, area 5.4mm2, adj f0,f1,f375,f377
  f377: extruded ~8x0.73mm, area 6mm2, adj f0,f1,f376,f378
  f378: extruded ~8x0.75mm, area 6mm2, adj f0,f1,f377,f379
  f379: extruded ~8x0.67mm, area 5.4mm2, adj f0,f1,f378,f380
  f380: extruded ~8x0.48mm, area 3.9mm2, adj f0,f1,f357,f379
  f381: extruded ~8x0.49mm, area 3.9mm2, adj f0,f1,f360,f382
  f382: extruded ~8x0.63mm, area 5.1mm2, adj f0,f1,f381,f383
  f383: extruded ~8x0.7mm, area 5.7mm2, adj f0,f1,f382,f384
  f384: extruded ~8x0.7mm, area 5.8mm2, adj f0,f1,f383,f385
  f385: extruded ~8x0.61mm, area 5.5mm2, adj f0,f1,f384,f386
  f386: extruded ~8x0.44mm, area 4.8mm2, adj f0,f1,f385,f387
  f387: extruded ~8x0.52mm, area 4.6mm2, adj f0,f1,f386,f388
  f388: extruded ~8x0.62mm, area 5mm2, adj f0,f1,f361,f387
PART B: 11 faces, bbox 22x35.8x10 mm
  f0: cylinder r=11mm len=22mm, axis (0,0,-1), area 86.8mm2, adj f1,f2,f5,f6
  f1: plane 35.8x22mm, normal (0,0,1), area 360.9mm2, adj f0,f3,f4,f5,f6,f7
  f2: plane 35.8x22mm, normal (0,0,-1), area 439.5mm2, adj f0,f3,f4,f5,f6
  f3: cylinder r=6mm len=12mm, axis (0,0,-1), area 44.2mm2, adj f1,f2,f5,f6
  f4: cylinder r=4.5mm len=9mm, axis (0,0,-1), area 38.2mm2, adj f1,f2
  f5: plane 2.57x1.35mm, normal (-1,0,0), area 3.5mm2, adj f0,f1,f2,f3
  f6: plane 2.57x1.35mm, normal (1,0,0), area 3.5mm2, adj f0,f1,f2,f3
  f7: cylinder r=5mm len=10mm, axis (0,0,-1), area 36.1mm2, adj f1,f8
  f8: plane 10x10mm, normal (0,0,1), area 29.5mm2, adj f7,f9
  f9: cylinder r=3.95mm len=7.9mm, axis (0,0,-1), area 186.1mm2, adj f8,f10
  f10: plane 7.9x7.9mm, normal (0,0,1), area 49mm2, adj f9
PLACE A t=(52.08,-6.71,0)mm
PLACE B rot(axis=(0,0,-1),80deg) t=(52.02,-6.59,-2)mm
MATE revolute B.f7 <-> A.f0  axis (0,0,1) through (52.02,-6.59,8)mm
